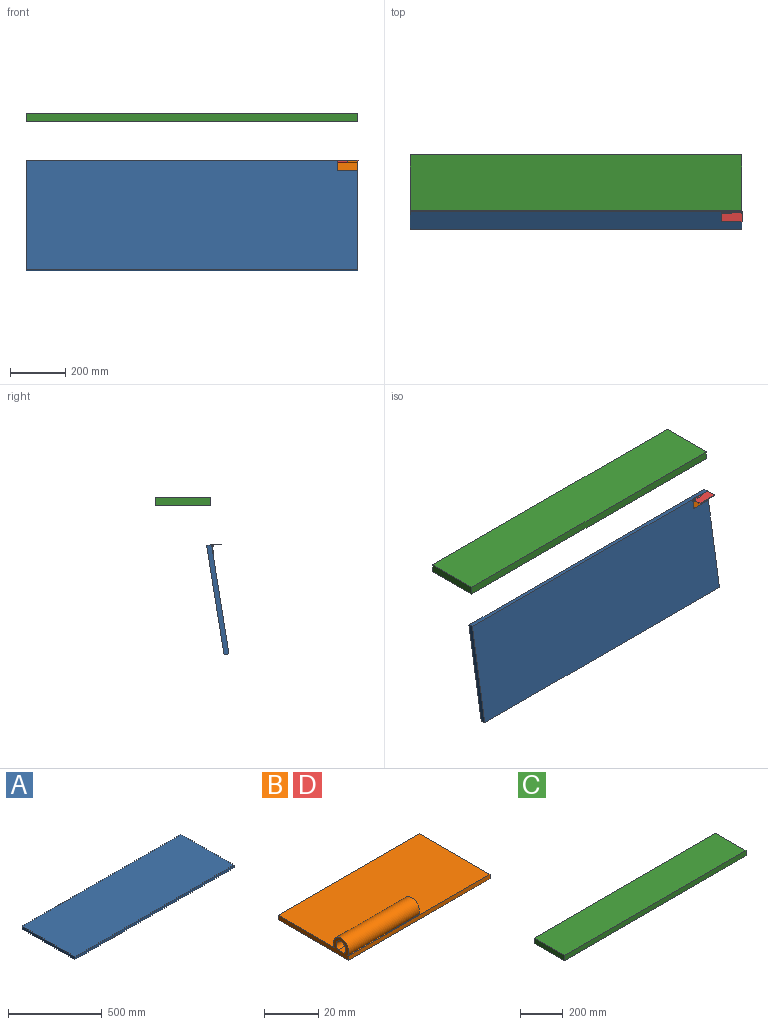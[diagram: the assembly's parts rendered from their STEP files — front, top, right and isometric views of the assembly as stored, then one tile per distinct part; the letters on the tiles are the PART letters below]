
ASSEMBLY  parts=4 mates=6
PART A: 6 faces, bbox 1200x400x18 mm
  f0: plane 1200x18mm, normal (0,1,0), area 21600mm2, adj f1,f3,f4,f5
  f1: plane 400x18mm, normal (-1,0,0), area 7200mm2, adj f0,f2,f4,f5
  f2: plane 1200x18mm, normal (0,-1,0), area 21600mm2, adj f1,f3,f4,f5
  f3: plane 400x18mm, normal (1,0,0), area 7200mm2, adj f0,f2,f4,f5
  f4: plane 1200x400mm, normal (0,0,1), area 480000mm2, adj f0,f1,f2,f3
  f5: plane 1200x400mm, normal (0,0,-1), area 480000mm2, adj f0,f1,f2,f3
PART B: 9 faces, bbox 74x37x8 mm
  f0: plane 74x2mm, normal (0,1,0), area 148mm2, adj f1,f3,f4,f5
  f1: plane 37x8mm, normal (-1,0,0), area 95.3mm2, adj f0,f2,f4,f5,f6,f7
  f2: plane 74x2mm, normal (0,-1,0), area 148mm2, adj f1,f3,f4,f5
  f3: plane 37x2mm, normal (1,0,0), area 74mm2, adj f0,f2,f4,f5
  f4: plane 74x37mm, normal (0,0,1), area 2597.8mm2, adj f0,f1,f2,f3,f6,f7,f8
  f5: plane 74x37mm, normal (0,0,-1), area 2738mm2, adj f0,f1,f2,f3
  f6: cylinder r=4mm len=37mm, axis (-1,0,0), area 619.9mm2, adj f1,f4,f8
  f7: cylinder r=2.54mm len=37mm, axis (-1,0,0), area 465.9mm2, adj f1,f4,f8
  f8: plane 8x6mm, normal (1,0,0), area 21.3mm2, adj f4,f6,f7
PART C: 6 faces, bbox 1200x200x30 mm
  f0: plane 200x30mm, normal (1,0,0), area 6000mm2, adj f1,f3,f4,f5
  f1: plane 1200x30mm, normal (0,1,0), area 36000mm2, adj f0,f2,f4,f5
  f2: plane 200x30mm, normal (-1,0,0), area 6000mm2, adj f1,f3,f4,f5
  f3: plane 1200x30mm, normal (0,-1,0), area 36000mm2, adj f0,f2,f4,f5
  f4: plane 1200x200mm, normal (0,0,1), area 240000mm2, adj f0,f1,f2,f3
  f5: plane 1200x200mm, normal (0,0,-1), area 240000mm2, adj f0,f1,f2,f3
PART D: same geometry as B
PLACE A rot(axis=(1,0,0),81deg) t=(-22.76,-52.72,67)mm
PLACE B rot(axis=(0,-0.65,0.76),180deg) t=(565.32,-102.65,-132.13)mm
PLACE C at identity fixed
PLACE D rot(axis=(1,0,0),180deg) t=(560.68,-95.61,-140.38)mm
MATE planar B.f1 <-> A.f3  axis (1,0,0) through (600,-108.39,-155.83)mm
MATE planar D.f3 <-> C.f0  axis (1,0,0) through (600,-123.16,-141.38)mm
MATE planar A.f4 <-> B.f5  axis (0,-0.99,0.16) through (0,-135.53,-338.57)mm
MATE planar B.f2 <-> A.f0  axis (0,0.16,0.99) through (563,-105.07,-140.91)mm
MATE planar D.f3 <-> B.f1  axis (1,0,0) through (600,-123.16,-141.38)mm
MATE cylindrical B.f6 <-> D.f6  axis (-1,0,0) through (563,-108.66,-144.38)mm
